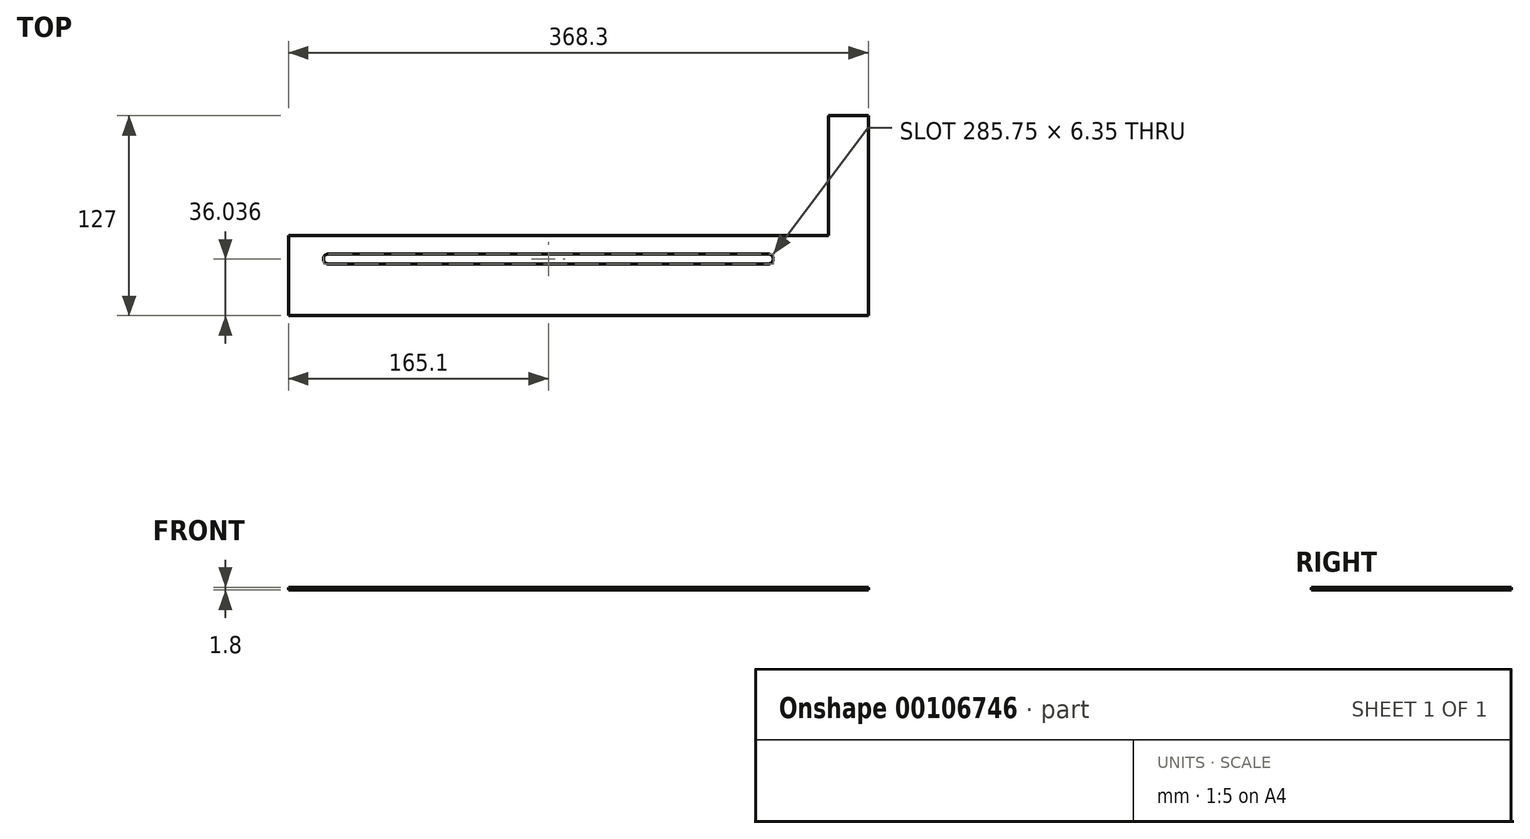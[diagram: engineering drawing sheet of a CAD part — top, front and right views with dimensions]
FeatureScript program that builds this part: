
annotation { "Feature Type Name" : "Feature", "Feature Type Description" : "" }
export const myFeature = defineFeature(function(context is Context, id is Id, definition is map)
    precondition{}
    {
        {
            var Q0;
            Q0=qCreatedBy(makeId("Right.planeOp"),FACE);
            var sketch = newSketch(context, id + "F0", { "sketchPlane" : qUnion([Q0])});
            skLineSegment(sketch, "E0.bottom", {"start": v(25.4, 0.9) * mm, "end": v(-25.4, 0.9) * mm});
            skLineSegment(sketch, "E0.top", {"start": v(25.4, -0.9) * mm, "end": v(-25.4, -0.9) * mm});
            skLineSegment(sketch, "E0.left", {"start": v(25.4, 0.9) * mm, "end": v(25.4, -0.9) * mm});
            skLineSegment(sketch, "E0.right", {"start": v(-25.4, 0.9) * mm, "end": v(-25.4, -0.9) * mm});
            skPoint(sketch, "E0.middle", {"position": v(0, 0) * mm});
            skSolve(sketch);
        }
        {
            var Q0;
            Q0=qSketchRegion(id+"F0",true);
            extrude(context, id + "F1", {"entities" : qUnion([Q0]), "depth" : 171.45 * mm, "hasSecondDirection" : true, "secondDirectionOppositeDirection" : true, "secondDirectionDepth" : 171.45 * mm});
        }
        {
            var Q0;
            Q0=makeQuery(id+"F1.opExtrude","SWEPT_FACE",FACE,{"disambiguationData":[OSD([sQuery(id+"F0.wireOp",EDGE,"E0.bottom")])]});
            var sketch = newSketch(context, id + "F2", { "sketchPlane" : qUnion([Q0])});
            skLineSegment(sketch, "E1", {"start": v(0, 0) * mm, "end": v(0, -25.4) * mm, "construction": true});
            skLineSegment(sketch, "E2", {"start": v(0, -25.4) * mm, "end": v(171.45, -25.4) * mm, "construction": true});
            skLineSegment(sketch, "E3", {"start": v(171.45, -25.4) * mm, "end": v(171.45, 101.6) * mm});
            skLineSegment(sketch, "E4", {"start": v(171.45, 101.6) * mm, "end": v(196.85, 101.6) * mm});
            skLineSegment(sketch, "E5", {"start": v(196.85, 101.6) * mm, "end": v(196.85, -25.4) * mm});
            skLineSegment(sketch, "E6", {"start": v(171.45, -25.4) * mm, "end": v(196.85, -25.4) * mm});
            skSolve(sketch);
        }
        {
            var Q0;
            Q0=qSketchRegion(id+"F2",true);
            extrude(context, id + "F3", {"entities" : qUnion([Q0]), "operationType" : NewBodyOperationType.ADD, "oppositeDirection" : true, "depth" : 1.8 * mm});
        }
        {
            var Q0;
            Q0=makeQuery(id+"F3.boolean.opBoolean","MERGE",FACE,{"derivedFrom":[makeQuery(id+"F1.opExtrude","SWEPT_FACE",FACE,{"disambiguationData":[OSD([sQuery(id+"F0.wireOp",EDGE,"E0.bottom")])]}),makeQuery(id+"F3.opExtrude","CAP_FACE",FACE,{"disambiguationData":[OSD([sQuery(id+"F2.wireOp",EDGE,"E3"),sQuery(id+"F2.wireOp",EDGE,"E4"),sQuery(id+"F2.wireOp",EDGE,"E5"),sQuery(id+"F2.wireOp",EDGE,"E6")])],"isStart":true})]});
            var sketch = newSketch(context, id + "F4", { "sketchPlane" : qUnion([Q0])});
            skLineSegment(sketch, "E7", {"start": v(-146.05, 10.64) * mm, "end": v(133.35, 10.64) * mm, "construction": true});
            skArc(sketch, "E8.0.startCap", {"start": v(-146.05, 7.46) * mm, "mid": v(-149.23, 10.64) * mm, "end": v(-146.05, 13.81) * mm});
            skArc(sketch, "E8.0.endCap", {"start": v(133.35, 13.81) * mm, "mid": v(136.53, 10.64) * mm, "end": v(133.35, 7.46) * mm});
            skLineSegment(sketch, "E8.0.left", {"start": v(-146.05, 13.81) * mm, "end": v(133.35, 13.81) * mm});
            skLineSegment(sketch, "E8.0.right", {"start": v(-146.05, 7.46) * mm, "end": v(133.35, 7.46) * mm});
            skSolve(sketch);
        }
        {
            var Q0;
            Q0=qSketchRegion(id+"F4",true);
            extrude(context, id + "F5", {"entities" : qUnion([Q0]), "operationType" : NewBodyOperationType.REMOVE, "endBound" : BoundingType.THROUGH_ALL, "oppositeDirection" : true, "depth" : 25.4 * mm});
        }
    });
